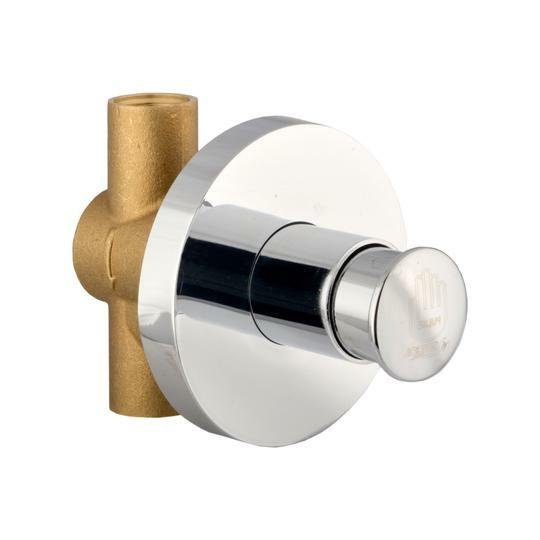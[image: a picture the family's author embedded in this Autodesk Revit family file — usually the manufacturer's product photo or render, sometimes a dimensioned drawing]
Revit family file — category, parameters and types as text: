
# Revit family: ID-PU01-11 VALVULA PUSH DUCHA GRICOL
name_source: partatom
category: Plumbing Fixtures
revit_build: Autodesk Revit 2018 (Build: 20170223_1515(x64)
units: mm (PartAtom-declared; Revit-internal decimal feet)

## family parameters
Cut with Voids When Loaded = No
Host = Face
OmniClass Number = 23.31.11.00
Part Type = Normal
Room Calculation Point = No
Round Connector Dimension = Use Diameter
Shared = No

## types (1)
- ID-PU01-11
    Alto = 86 mm  [stored 0.282152 ft]
    Ancho = 118.5 mm
    Buje = 34.2 mm
    CW Connection = Yes
    Default Elevation = 0 mm  [stored 0 ft]
    Description = Valvula
    Escudo = 120 mm
    HW Connection = Yes
    Laton = Laton
    Link Ficha Tecnica = http://infotecnica.gricol.com
    Manufacturer = Gricol
    Metal - ABS Cromado = Plastico - ABS Cromado
    Metal - Acero inoxidable = Metal - Acero inoxidable
    Model = ID-PU01-11
    Product Name = VALVULA PUSH DUCHA GRICOL
    Type Image = <None>
    URL = https://www.gricol.com
    Vent Connection = No
    Waste Connection = No

note: [stored X ft] marks values corroborated as IEEE doubles in the binary element streams (Revit-internal decimal feet)

## geometry (parser evidence)
native form markers: Blend x2, Sweep x6
no freeform markers — native parametric forms only
